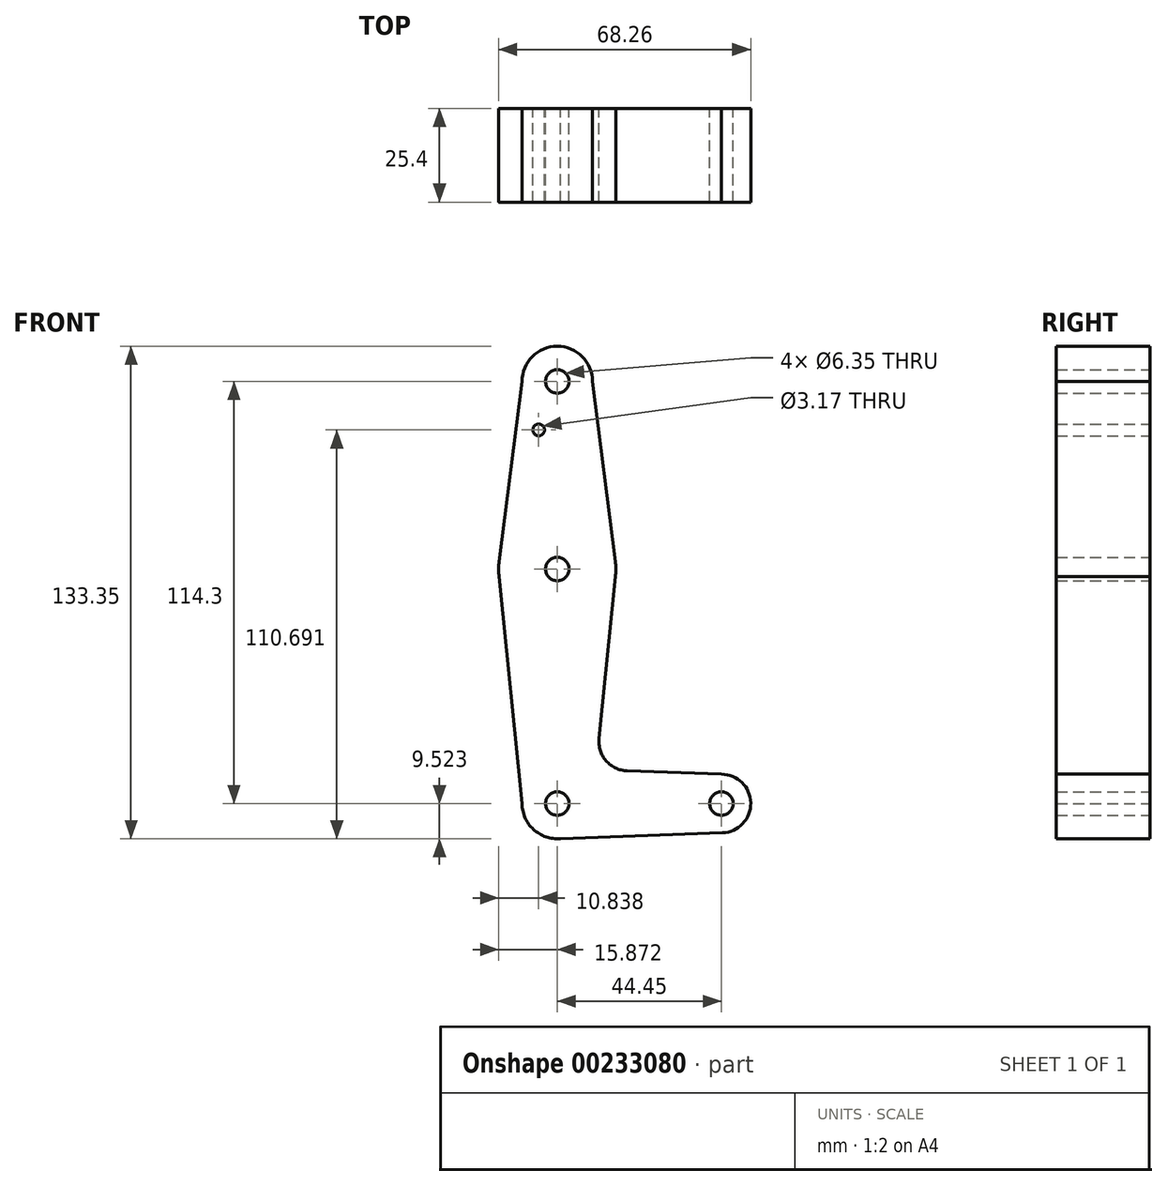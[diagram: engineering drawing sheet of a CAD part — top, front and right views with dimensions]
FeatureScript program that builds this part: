
annotation { "Feature Type Name" : "Feature", "Feature Type Description" : "" }
export const myFeature = defineFeature(function(context is Context, id is Id, definition is map)
    precondition{}
    {
        {
            var Q0;
            Q0=qCreatedBy(makeId("Front.planeOp"),FACE);
            var sketch = newSketch(context, id + "F0", { "sketchPlane" : qUnion([Q0])});
            skCircle(sketch, "E0", {"center": v(-53.4, 66.08) * mm, "radius": 9.53 * mm});
            skCircle(sketch, "E1", {"center": v(-53.4, -48.22) * mm, "radius": 9.53 * mm});
            skCircle(sketch, "E2", {"center": v(-53.4, 15.28) * mm, "radius": 15.88 * mm});
            skLineSegment(sketch, "E3", {"start": v(-53.4, -48.22) * mm, "end": v(-8.96, -48.22) * mm});
            skCircle(sketch, "E4", {"center": v(-8.96, -48.22) * mm, "radius": 7.94 * mm});
            skLineSegment(sketch, "E5", {"start": v(-53.4, 66.08) * mm, "end": v(-53.4, -48.22) * mm});
            skLineSegment(sketch, "E6", {"start": v(-62.93, 66.08) * mm, "end": v(-69.16, 17.3) * mm});
            skLineSegment(sketch, "E7", {"start": v(-43.88, 66.08) * mm, "end": v(-37.66, 17.3) * mm});
            skLineSegment(sketch, "E8", {"start": v(-69.16, 13.27) * mm, "end": v(-62.93, -48.22) * mm});
            skLineSegment(sketch, "E9", {"start": v(-37.66, 13.27) * mm, "end": v(-42.1, -30.62) * mm});
            skLineSegment(sketch, "E10", {"start": v(-34.48, -39.37) * mm, "end": v(-8.96, -40.28) * mm});
            skCircle(sketch, "E11", {"center": v(-53.4, 66.08) * mm, "radius": 3.18 * mm});
            skCircle(sketch, "E12", {"center": v(-53.4, 15.28) * mm, "radius": 3.18 * mm});
            skCircle(sketch, "E13", {"center": v(-53.4, -48.22) * mm, "radius": 3.18 * mm});
            skCircle(sketch, "E14", {"center": v(-8.96, -48.22) * mm, "radius": 3.18 * mm});
            skCircle(sketch, "E15", {"center": v(-58.44, 52.95) * mm, "radius": 1.59 * mm});
            skPoint(sketch, "E16.newPointA", {"position": v(-43.88, -48.22) * mm});
            skArc(sketch, "E16.filletArc", {"start": v(-42.1, -30.62) * mm, "mid": v(-40.18, -36.65) * mm, "end": v(-34.48, -39.37) * mm});
            skLineSegment(sketch, "E17", {"start": v(-53.56, -57.74) * mm, "end": v(-8.68, -56.15) * mm});
            skSolve(sketch);
        }
        {
            var Q0;
            Q0 = qSketchRegion(id + "F0", true);
            var Q1;
            {var subQ0=sQuery(id+"F0.wireOp",EDGE,"E5");var subQ1=sQuery(id+"F0.wireOp",EDGE,"E1");var subQ2=makeQuery(id+"F0.imprint","INTERSECT",VERTEX,{"derivedFrom":[subQ1,subQ0]});Q1=makeQuery(id+"F0.imprint","IMPRINT",FACE,{"disambiguationData":[TD([[makeQuery(id+"F0.imprint","IMPRINT",EDGE,{"disambiguationData":[TD([[subQ2,1.0]])],"derivedFrom":subQ1}),1.0]])]});}
            extrude(context, id + "F1", {"entities" : qUnion([Q0, Q1]), "depth" : 25.4 * mm});
        }
    });
